# Revit family: BISLEY_BS_Filing_Cabinets
name_source: partatom
category: Furniture
revit_build: Autodesk Revit 2018 (Build: 20180423_1000(x64)
units: mm (PartAtom-declared; Revit-internal decimal feet)

## family parameters
Always vertical = Yes
Cut with Voids When Loaded = No
OmniClass Number = 23.40.20.00
OmniClass Title = General Furniture and Specialties
Room Calculation Point = No
Shared = No
Work Plane-Based = No

## types (7) — shared parameters
Category = Furniture
Compliance Standards Certification = BS 4875: Part 8: 1985, BS 4875: Part 7: 1985
Depth = 622 mm  [stored 2.04068 ft]
Finish = Powder Coated
Label position = 135 mm
Manufacturer = Bisley
Material = Steel
Model = Bisley Filing Cabinet
Range = BS Filing Cabinet
Routine Maintenance = We recommend you clean your unit with warm water and a mild detergent solution. A damp cloth can be used to remove dust particles.
URL = www.bisley.com
Uniclass 2015 Code = PR_40_30_29
Uniclass2015Title = Shelves and Storage Units
Uniclass2015Version = V1.1
Warranty = 7 years from date of purchase

## per-type parameters (varying)
| type | 1623-1643 Visibility | 1653 Visibility | 3rd label vis | 4th label vis | Description | Dimensions | Drawer width1 | Drawer width2 | Height | Label right | Lebel left | Model Reference | Number of drawers | Product Information | Weight | Width | plinth height |
| 1623 | Yes | No | No | No | 2 Drawer Cabinet | 711 x 470 x 622 mm | 213 mm  [stored 0.698819 ft] | -213 mm  [stored -0.698819 ft] | 711 mm | Yes | No | 1623 | 2 | 2 Drawer Cabinet | 25.76kg | 470 mm  [stored 1.54199 ft] | 70 mm  [stored 0.229659 ft] |
| 1633 | Yes | No | Yes | No | 3 Drawer Cabinet | 1016 x 470 x 622 mm | 213 mm  [stored 0.698819 ft] | -213 mm  [stored -0.698819 ft] | 1016 mm | Yes | No | 1633 | 3 | 3 Drawer Cabinet | 41.87kg | 470 mm  [stored 1.54199 ft] | 70 mm  [stored 0.229659 ft] |
| 1643 | Yes | No | Yes | Yes | 4 Door Cabinet | 1321 x 470 x 622 mm | 213 mm  [stored 0.698819 ft] | -213 mm  [stored -0.698819 ft] | 1321 mm  [stored 4.33399 ft] | Yes | No | 1643 | 4 | 4 Door Cabinet | 47.90kg | 470 mm  [stored 1.54199 ft] | 70 mm  [stored 0.229659 ft] |
| 1653 | No | Yes | No | No | 5 Drawer Cabinet | 1511x 470 x 622 mm | 213 mm  [stored 0.698819 ft] | -213 mm  [stored -0.698819 ft] | 1511 mm  [stored 4.95735 ft] | Yes | No | 1653 | 5 | 5 Drawer Cabinet | 67.72kg | 470 mm  [stored 1.54199 ft] | 50 mm  [stored 0.164042 ft] |
| 3623 | Yes | No | No | No | 2 Drawer Cabinet | 711 x 413 x 622 mm | 185 mm | -185 mm | 711 mm | No | Yes | 3623 | 2 | 2 Drawer Cabinet | 28.94kg | 413 mm  [stored 1.35499 ft] | 70 mm  [stored 0.229659 ft] |
| 3633 | Yes | No | Yes | No | 3 Drawer Cabinet | 1016 x 470 x 622 mm | 185 mm | -185 mm | 1016 mm | No | Yes | 1633 | 3 | 3 Drawer Cabinet | 39.94kg | 413 mm  [stored 1.35499 ft] | 70 mm  [stored 0.229659 ft] |
| 3643 | Yes | No | Yes | Yes | 4 Drawer Cabinet | 1321 x 470 x 622 mm | 185 mm | -185 mm | 1321 mm  [stored 4.33399 ft] | No | Yes | 1643 | 4 | 4 Drawer Cabinet | 51.16kg | 413 mm  [stored 1.35499 ft] | 70 mm  [stored 0.229659 ft] |

note: [stored X ft] marks values corroborated as IEEE doubles in the binary element streams (Revit-internal decimal feet)

## geometry (parser evidence)
native form markers: Sweep x2
no freeform markers — native parametric forms only
